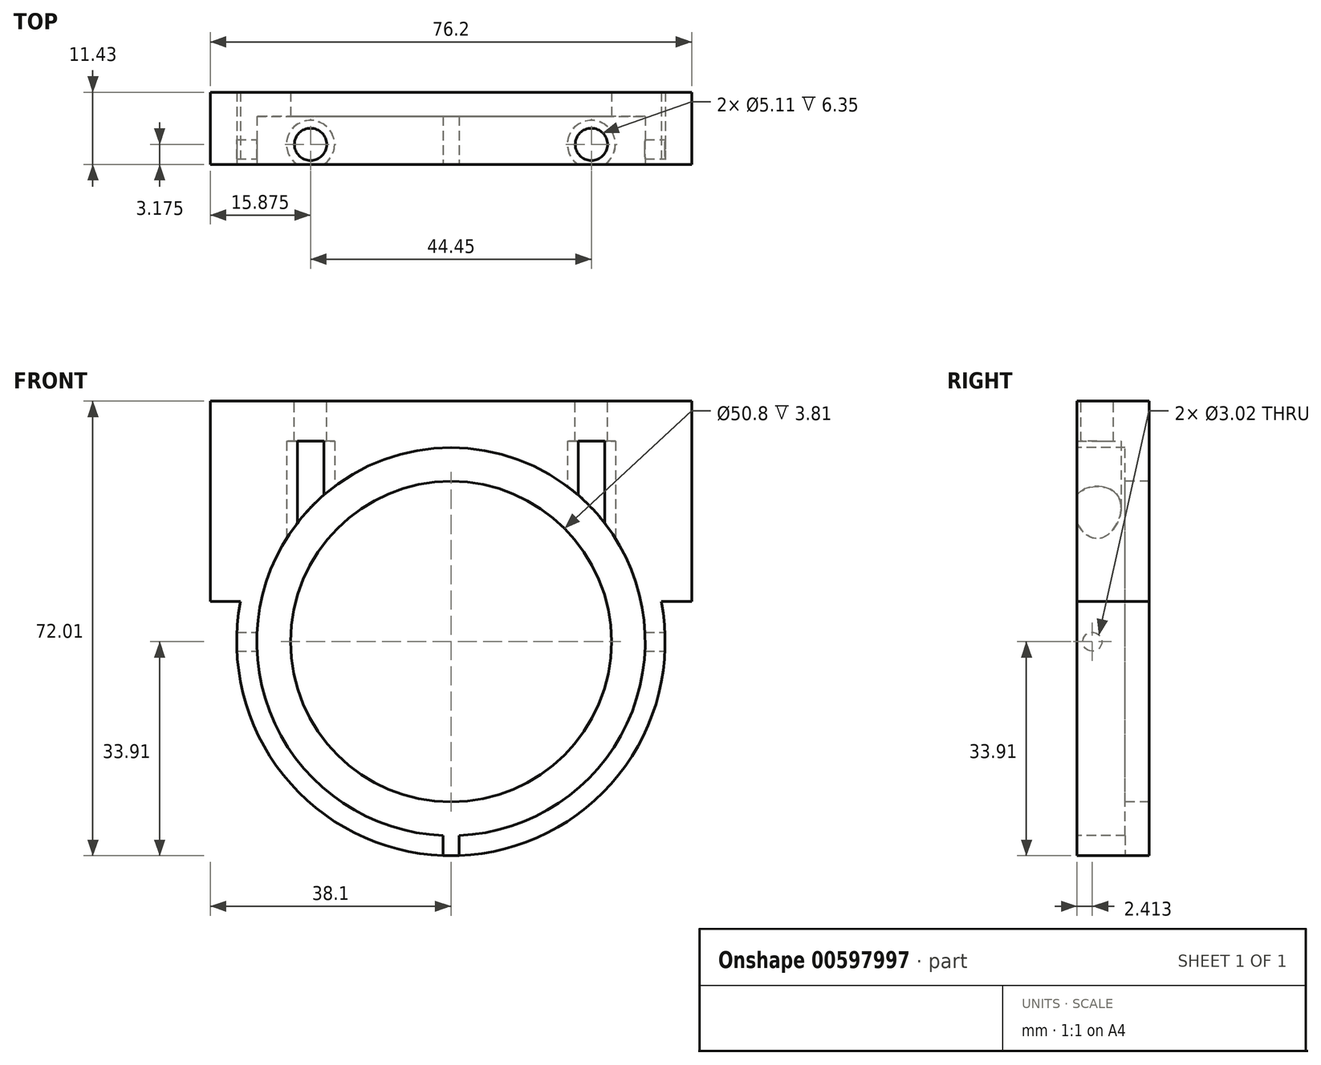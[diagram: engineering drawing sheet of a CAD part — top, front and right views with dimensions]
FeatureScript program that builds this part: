
annotation { "Feature Type Name" : "Feature", "Feature Type Description" : "" }
export const myFeature = defineFeature(function(context is Context, id is Id, definition is map)
    precondition{}
    {
        {
            var Q0;
            Q0=qCreatedBy(makeId("Front.planeOp"),FACE);
            var sketch = newSketch(context, id + "F0", { "sketchPlane" : qUnion([Q0])});
            skCircle(sketch, "E0", {"center": v(0, 0) * mm, "radius": 33.9 * mm});
            skSolve(sketch);
        }
        {
            var Q0;
            Q0=qSketchRegion(id+"F0",true);
            extrude(context, id + "F1", {"entities" : qUnion([Q0]), "depth" : -11.43 * mm, "offsetDistance" : 25.4 * mm});
        }
        {
            var Q0;
            Q0=makeQuery(id+"F1.opExtrude","CAP_FACE",FACE,{"disambiguationData":[OSD([sQuery(id+"F0.wireOp",EDGE,"E0")])],"isStart":true});
            var sketch = newSketch(context, id + "F2", { "sketchPlane" : qUnion([Q0])});
            skCircle(sketch, "E1", {"center": v(0, 0) * mm, "radius": 30.73 * mm});
            skSolve(sketch);
        }
        {
            var Q0;
            Q0=qSketchRegion(id+"F2",true);
            extrude(context, id + "F3", {"entities" : qUnion([Q0]), "operationType" : NewBodyOperationType.REMOVE, "oppositeDirection" : true, "depth" : 7.62 * mm});
        }
        {
            var Q0;
            Q0=makeQuery(id+"F3.boolean.opBoolean","COPY",FACE,{"derivedFrom":makeQuery(id+"F3.opExtrude","CAP_FACE",FACE,{"disambiguationData":[OSD([sQuery(id+"F2.wireOp",EDGE,"E1")])],"isStart":false})});
            var sketch = newSketch(context, id + "F4", { "sketchPlane" : qUnion([Q0])});
            skLineSegment(sketch, "E2", {"start": v(-2.93, 21.78) * mm, "end": v(-2.93, 21.78) * mm});
            skLineSegment(sketch, "E3", {"start": v(-2.93, -21.78) * mm, "end": v(-2.93, -21.78) * mm});
            skCircle(sketch, "E4", {"center": v(0, 0) * mm, "radius": 25.4 * mm});
            skSolve(sketch);
        }
        {
            var Q0;
            Q0=qSketchRegion(id+"F4",true);
            extrude(context, id + "F5", {"entities" : qUnion([Q0]), "operationType" : NewBodyOperationType.REMOVE, "oppositeDirection" : true, "depth" : 25.4 * mm});
        }
        {
            var Q0;
            Q0=qCreatedBy(makeId("Right.planeOp"),FACE);
            cPlane(context, id + "F6", {"entities" : qUnion([Q0]), "cplaneType" : CPlaneType.OFFSET, "offset" : 254 * mm, "width" : 152.4 * mm, "height" : 152.4 * mm});
        }
        {
            var Q0;
            Q0=qCreatedBy(id+"F6.planeOp",FACE);
            var sketch = newSketch(context, id + "F7", { "sketchPlane" : qUnion([Q0])});
            skCircle(sketch, "E5", {"center": v(2.41, 0) * mm, "radius": 1.51 * mm});
            skSolve(sketch);
        }
        {
            var Q0;
            Q0=makeQuery(id+"F1.opExtrude","CAP_FACE",FACE,{"disambiguationData":[OSD([sQuery(id+"F0.wireOp",EDGE,"E0")])],"isStart":true});
            var sketch = newSketch(context, id + "F8", { "sketchPlane" : qUnion([Q0])});
            skLineSegment(sketch, "E6", {"start": v(-1.27, -30.7) * mm, "end": v(-1.27, -33.89) * mm});
            skLineSegment(sketch, "E7", {"start": v(1.27, -33.89) * mm, "end": v(1.27, -30.7) * mm});
            skLineSegment(sketch, "E8", {"start": v(-1.27, -30.7) * mm, "end": v(1.27, -30.7) * mm});
            skLineSegment(sketch, "E9", {"start": v(-1.27, -33.89) * mm, "end": v(0, -35.86) * mm});
            skLineSegment(sketch, "E10", {"start": v(0, -35.86) * mm, "end": v(1.27, -33.89) * mm});
            skSolve(sketch);
        }
        {
            var Q0;
            Q0=qSketchRegion(id+"F8",true);
            extrude(context, id + "F9", {"entities" : qUnion([Q0]), "operationType" : NewBodyOperationType.REMOVE, "oppositeDirection" : true, "depth" : 7.62 * mm, "offsetDistance" : 25.4 * mm});
        }
        {
            var Q0;
            Q0=makeQuery(id+"F1.opExtrude","CAP_FACE",FACE,{"disambiguationData":[OSD([sQuery(id+"F0.wireOp",EDGE,"E0")])],"isStart":true});
            var sketch = newSketch(context, id + "F10", { "sketchPlane" : qUnion([Q0])});
            skArc(sketch, "E11", {"start": v(33.9, 0) * mm, "mid": v(0, 33.9) * mm, "end": v(-33.9, 0) * mm});
            skLineSegment(sketch, "E12", {"start": v(-33.9, 0) * mm, "end": v(-38.1, 0) * mm, "construction": true});
            skLineSegment(sketch, "E13", {"start": v(-38.1, 0) * mm, "end": v(-38.1, 38.1) * mm});
            skLineSegment(sketch, "E14", {"start": v(-38.1, 38.1) * mm, "end": v(38.1, 38.1) * mm});
            skLineSegment(sketch, "E15", {"start": v(38.1, 38.1) * mm, "end": v(38.1, 0) * mm});
            skLineSegment(sketch, "E16", {"start": v(38.1, 0) * mm, "end": v(33.9, 0) * mm, "construction": true});
            skLineSegment(sketch, "E17", {"start": v(38.1, 6.35) * mm, "end": v(33.3, 6.35) * mm});
            skLineSegment(sketch, "E18", {"start": v(-38.1, 6.35) * mm, "end": v(-33.3, 6.35) * mm});
            skSolve(sketch);
        }
        {
            var Q0;
            Q0=makeQuery(id+"F10.imprint","IMPRINT",FACE,{"disambiguationData":[TD([[makeQuery(id+"F10.imprint","IMPRINT",EDGE,{"derivedFrom":sQuery(id+"F10.wireOp",EDGE,"E11")}),-1.0]])]});
            var Q1;
            Q1=makeQuery(id+"F1.opExtrude","CAP_FACE",FACE,{"disambiguationData":[OSD([sQuery(id+"F0.wireOp",EDGE,"E0")])],"isStart":false});
            extrude(context, id + "F11", {"entities" : qUnion([Q0]), "operationType" : NewBodyOperationType.ADD, "endBound" : BoundingType.UP_TO_SURFACE, "oppositeDirection" : true, "depth" : 25.4 * mm, "endBoundEntityFace" : qUnion([Q1]), "offsetDistance" : 25.4 * mm});
        }
        {
            var Q0;
            Q0=qSketchRegion(id+"F7",true);
            extrude(context, id + "F12", {"entities" : qUnion([Q0]), "operationType" : NewBodyOperationType.REMOVE, "oppositeDirection" : true, "depth" : 2540 * mm, "offsetDistance" : 25.4 * mm});
        }
        {
            var Q0;
            Q0=makeQuery(id+"F11.opExtrude","SWEPT_FACE",FACE,{"disambiguationData":[OSD([sQuery(id+"F10.wireOp",EDGE,"E14")])]});
            var sketch = newSketch(context, id + "F13", { "sketchPlane" : qUnion([Q0])});
            skLineSegment(sketch, "E19", {"start": v(22.23, 3.18) * mm, "end": v(0, 3.17) * mm, "construction": true});
            skLineSegment(sketch, "E20", {"start": v(0, 3.18) * mm, "end": v(-22.23, 3.17) * mm, "construction": true});
            skLineSegment(sketch, "E21", {"start": v(0, 0) * mm, "end": v(0, 11.43) * mm, "construction": true});
            skCircle(sketch, "E22", {"center": v(-22.23, 3.17) * mm, "radius": 2.55 * mm});
            skCircle(sketch, "E23", {"center": v(22.23, 3.18) * mm, "radius": 2.55 * mm});
            skSolve(sketch);
        }
        {
            var Q0;
            Q0 = qSketchRegion(id + "F13", true);
            extrude(context, id + "F14", {"entities" : qUnion([Q0]), "operationType" : NewBodyOperationType.REMOVE, "oppositeDirection" : true, "depth" : 25.4 * mm, "offsetDistance" : 25.4 * mm});
        }
        {
            var Q0;
            Q0=makeQuery(id+"F11.opExtrude","SWEPT_FACE",FACE,{"disambiguationData":[OSD([sQuery(id+"F10.wireOp",EDGE,"E18")])]});
            var sketch = newSketch(context, id + "F15", { "sketchPlane" : qUnion([Q0])});
            skCircle(sketch, "E24", {"center": v(22.23, -3.18) * mm, "radius": 3.81 * mm});
            skCircle(sketch, "E25", {"center": v(-22.23, -3.17) * mm, "radius": 3.81 * mm});
            skSolve(sketch);
        }
        {
            var Q0;
            Q0 = qSketchRegion(id + "F15", true);
            extrude(context, id + "F16", {"entities" : qUnion([Q0]), "operationType" : NewBodyOperationType.REMOVE, "oppositeDirection" : true, "depth" : 25.4 * mm, "offsetDistance" : 25.4 * mm});
        }
    });
